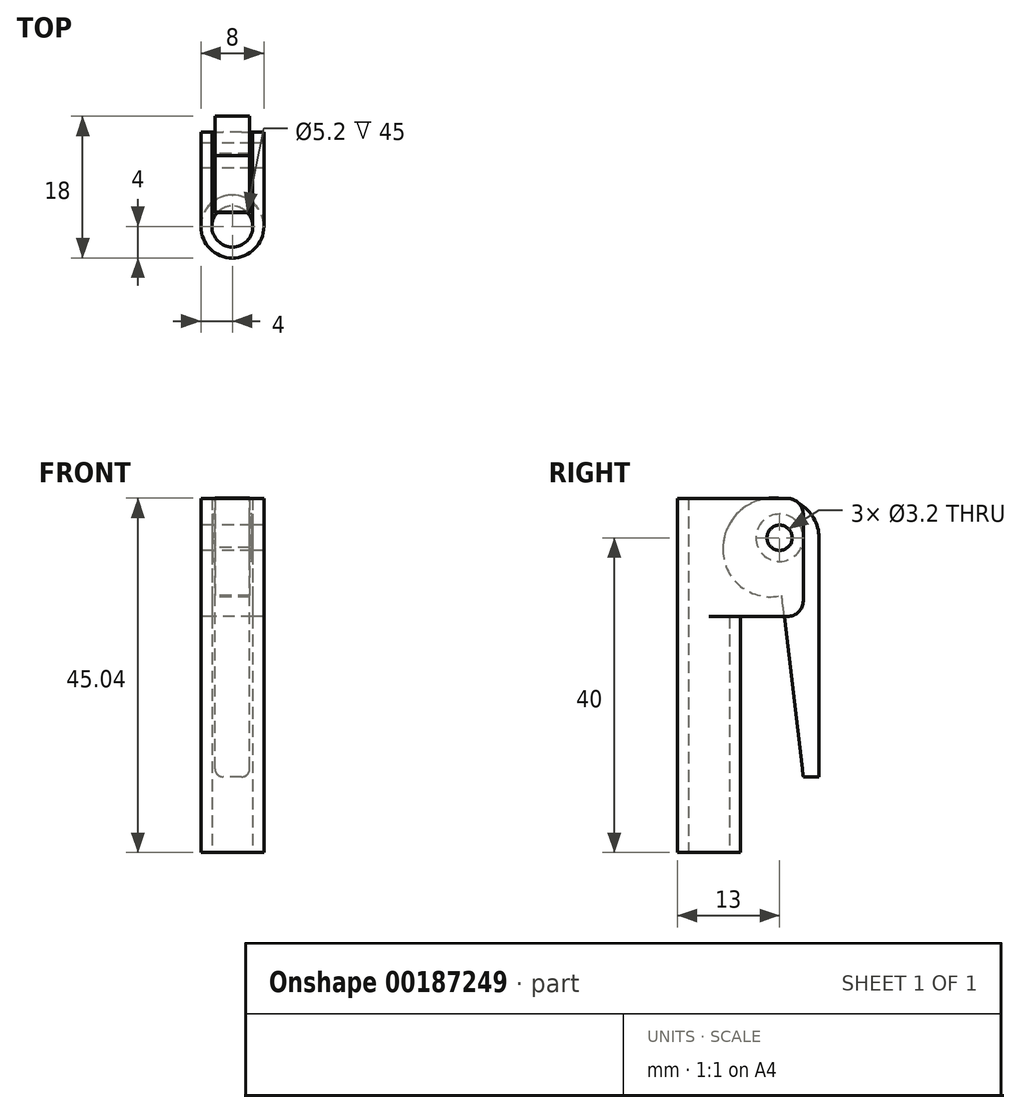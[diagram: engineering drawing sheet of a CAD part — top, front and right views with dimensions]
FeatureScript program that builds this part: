
annotation { "Feature Type Name" : "Feature", "Feature Type Description" : "" }
export const myFeature = defineFeature(function(context is Context, id is Id, definition is map)
    precondition{}
    {
        {
            var Q0;
            Q0=qCreatedBy(makeId("Top.planeOp"),FACE);
            var sketch = newSketch(context, id + "F0", { "sketchPlane" : qUnion([Q0])});
            skCircle(sketch, "E0", {"center": v(0, 0) * mm, "radius": 2.6 * mm});
            skCircle(sketch, "E1", {"center": v(0, 0) * mm, "radius": 4 * mm});
            skLineSegment(sketch, "E2", {"start": v(0, 0) * mm, "end": v(0, 5.84) * mm, "construction": true});
            skSolve(sketch);
        }
        {
            var Q0;
            Q0=makeQuery(id+"F0.imprint","IMPRINT",FACE,{"disambiguationData":[TD([[makeQuery(id+"F0.imprint","IMPRINT",EDGE,{"derivedFrom":sQuery(id+"F0.wireOp",EDGE,"E0")}),-1.0]])]});
            extrude(context, id + "F1", {"entities" : qUnion([Q0]), "depth" : 30 * mm});
        }
        {
            var Q0;
            Q0=makeQuery(id+"F1.opExtrude","CAP_FACE",FACE,{"disambiguationData":[OSD([sQuery(id+"F0.wireOp",EDGE,"E0"),sQuery(id+"F0.wireOp",EDGE,"E1")])],"isStart":false});
            var sketch = newSketch(context, id + "F2", { "sketchPlane" : qUnion([Q0])});
            skArc(sketch, "E3", {"start": v(-2.6, 0) * mm, "mid": v(0, -2.6) * mm, "end": v(2.6, 0) * mm});
            skArc(sketch, "E4", {"start": v(-2.6, 3.04) * mm, "mid": v(0, -4) * mm, "end": v(2.6, 3.04) * mm});
            skLineSegment(sketch, "E5", {"start": v(-4, 0) * mm, "end": v(-4, 12) * mm});
            skLineSegment(sketch, "E6", {"start": v(4, 0) * mm, "end": v(4, 12) * mm});
            skLineSegment(sketch, "E7.0", {"start": v(-2.6, 0) * mm, "end": v(-2.6, 12) * mm});
            skLineSegment(sketch, "E8.0", {"start": v(2.6, 0) * mm, "end": v(2.6, 12) * mm});
            skLineSegment(sketch, "E9", {"start": v(-2.6, 12) * mm, "end": v(-4, 12) * mm});
            skLineSegment(sketch, "E10", {"start": v(4, 12) * mm, "end": v(2.6, 12) * mm});
            skSolve(sketch);
        }
        {
            var Q0;
            {var subQ8=sQuery(id+"F2.wireOp",EDGE,"E3");Q0=makeQuery(id+"F2.imprint","IMPRINT",FACE,{"disambiguationData":[TD([[makeQuery(id+"F2.imprint","IMPRINT",EDGE,{"derivedFrom":subQ8}),-1.0]])]});}
            var Q1;
            {var subQ0=sQuery(id+"F2.wireOp",EDGE,"E6");Q1=makeQuery(id+"F2.imprint","IMPRINT",FACE,{"disambiguationData":[TD([[makeQuery(id+"F2.imprint","IMPRINT",EDGE,{"derivedFrom":subQ0}),1.0]])]});}
            var Q2;
            {var subQ0=sQuery(id+"F2.wireOp",EDGE,"E5");Q2=makeQuery(id+"F2.imprint","IMPRINT",FACE,{"disambiguationData":[TD([[makeQuery(id+"F2.imprint","IMPRINT",EDGE,{"derivedFrom":subQ0}),-1.0]])]});}
            extrude(context, id + "F3", {"entities" : qUnion([Q0, Q1, Q2]), "operationType" : NewBodyOperationType.ADD, "depth" : 15 * mm});
        }
        {
            var Q0;
            Q0=makeQuery(id+"F3.opExtrude","SWEPT_FACE",FACE,{"disambiguationData":[OSD([sQuery(id+"F2.wireOp",EDGE,"E6")])]});
            var sketch = newSketch(context, id + "F4", { "sketchPlane" : qUnion([Q0])});
            skSolve(sketch);
        }
        {
            var Q0;
            {var subQ0=sQuery(id+"F2.wireOp",EDGE,"E6");Q0=makeQuery(id+"F4.imprint","IMPRINT",FACE,{"disambiguationData":[TD([[makeQuery(id+"F4.imprint","IMPRINT",EDGE,{"derivedFrom":makeQuery(id+"F3.opExtrude","CAP_EDGE",EDGE,{"disambiguationData":[OSD([subQ0])],"isStart":true})}),1.0]])]});}
            var sketch = newSketch(context, id + "F5", { "sketchPlane" : qUnion([Q0])});
            skLineSegment(sketch, "E11", {"start": v(4, 0) * mm, "end": v(4, 56.04) * mm, "construction": true});
            skLineSegment(sketch, "E12", {"start": v(0, 50) * mm, "end": v(13.63, 50) * mm, "construction": true});
            skLineSegment(sketch, "E13", {"start": v(4, 40) * mm, "end": v(14, 40) * mm, "construction": true});
            skCircle(sketch, "E14", {"center": v(9, 40) * mm, "radius": 1.6 * mm});
            skSolve(sketch);
        }
        {
            var Q0;
            Q0=sQuery(id+"F5.wireOp",VERTEX,"E14.center");
            var Q1;
            Q1=makeQuery(id+"F1.opExtrude","SWEPT_BODY",BODY,{"disambiguationData":[OSD([sQuery(id+"F0.wireOp",EDGE,"E0"),sQuery(id+"F0.wireOp",EDGE,"E1")])]});
            hole(context, id + "F6", {"style" : HoleStyle.SIMPLE, "endStyle" : HoleEndStyle.THROUGH, "holeDiameter" : 3.2 * mm, "locations" : qUnion([Q0]), "scope" : qUnion([Q1]), "isTappedThrough" : true, "startStyle" : HoleStartStyle.PART});
        }
        {
            var Q0;
            Q0=qCreatedBy(makeId("Right.planeOp"),FACE);
            var sketch = newSketch(context, id + "F7", { "sketchPlane" : qUnion([Q0])});
            skLineSegment(sketch, "E15", {"start": v(9, 0) * mm, "end": v(9, 49.55) * mm, "construction": true});
            skLineSegment(sketch, "E16", {"start": v(0, 40) * mm, "end": v(31.34, 40) * mm, "construction": true});
            skCircle(sketch, "E17", {"center": v(9, 40) * mm, "radius": 1.6 * mm});
            skCircle(sketch, "E18", {"center": v(9, 40) * mm, "radius": 5 * mm});
            skLineSegment(sketch, "E19", {"start": v(12, 9.63) * mm, "end": v(14, 9.63) * mm});
            skLineSegment(sketch, "E20", {"start": v(14, 9.63) * mm, "end": v(14, 40) * mm});
            skLineSegment(sketch, "E21", {"start": v(9.02, 9.48) * mm, "end": v(9, 9.7) * mm});
            skArc(sketch, "E22", {"start": v(6.58, 44.37) * mm, "mid": v(1.95, 37.15) * mm, "end": v(9.27, 32.68) * mm});
            skLineSegment(sketch, "E23", {"start": v(12, 9.63) * mm, "end": v(9, 35) * mm});
            skArc(sketch, "E24", {"start": v(9, 45) * mm, "mid": v(4.02, 43.46) * mm, "end": v(1.8, 38.74) * mm});
            skSolve(sketch);
        }
        {
            var Q0;
            Q0=makeQuery(id+"F7.imprint","IMPRINT",FACE,{"disambiguationData":[TD([[makeQuery(id+"F7.imprint","IMPRINT",EDGE,{"derivedFrom":sQuery(id+"F7.wireOp",EDGE,"E19")}),1.0]])]});
            var Q1;
            Q1=makeQuery(id+"F7.imprint","IMPRINT",FACE,{"disambiguationData":[TD([[makeQuery(id+"F7.imprint","IMPRINT",EDGE,{"derivedFrom":sQuery(id+"F7.wireOp",EDGE,"E17")}),-1.0]])]});
            var Q2;
            {var subQ3=sQuery(id+"F7.wireOp",EDGE,"E22");Q2=makeQuery(id+"F7.imprint","IMPRINT",FACE,{"disambiguationData":[TD([[makeQuery(id+"F7.imprint","IMPRINT",EDGE,{"derivedFrom":subQ3}),1.0]])]});}
            var Q3;
            {var subQ3=sQuery(id+"F7.wireOp",EDGE,"E24");Q3=makeQuery(id+"F7.imprint","IMPRINT",FACE,{"disambiguationData":[TD([[makeQuery(id+"F7.imprint","IMPRINT",EDGE,{"derivedFrom":subQ3}),1.0]])]});}
            extrude(context, id + "F8", {"entities" : qUnion([Q0, Q1, Q2, Q3]), "depth" : 4.4 * mm, "symmetric" : true});
        }
        {
            var Q0;
            Q0=makeQuery(id+"F8.opExtrude","CAP_FACE",FACE,{"disambiguationData":[OSD([sQuery(id+"F7.wireOp",EDGE,"E17"),sQuery(id+"F7.wireOp",EDGE,"E18"),sQuery(id+"F7.wireOp",EDGE,"E19"),sQuery(id+"F7.wireOp",EDGE,"E20"),sQuery(id+"F7.wireOp",EDGE,"HUSRrBSV-6zhb-J2nK-oxZC-g73eNEfcQnkW")])],"isStart":false});
            var sketch = newSketch(context, id + "F9", { "sketchPlane" : qUnion([Q0])});
            skCircle(sketch, "E25", {"center": v(9, 40) * mm, "radius": 3 * mm});
            skSolve(sketch);
        }
        {
            var Q0;
            Q0=makeQuery(id+"F9.imprint","IMPRINT",FACE,{"disambiguationData":[TD([[makeQuery(id+"F9.imprint","IMPRINT",EDGE,{"derivedFrom":sQuery(id+"F9.wireOp",EDGE,"E25")}),1.0]])]});
            extrude(context, id + "F10", {"entities" : qUnion([Q0]), "operationType" : NewBodyOperationType.ADD, "depth" : 0.3 * mm});
        }
        {
            var Q0;
            Q0=makeQuery(id+"F8.opExtrude","CAP_FACE",FACE,{"disambiguationData":[OSD([sQuery(id+"F7.wireOp",EDGE,"E17"),sQuery(id+"F7.wireOp",EDGE,"E18"),sQuery(id+"F7.wireOp",EDGE,"E19"),sQuery(id+"F7.wireOp",EDGE,"E20"),sQuery(id+"F7.wireOp",EDGE,"HUSRrBSV-6zhb-J2nK-oxZC-g73eNEfcQnkW")])],"isStart":true});
            var sketch = newSketch(context, id + "F11", { "sketchPlane" : qUnion([Q0])});
            skCircle(sketch, "E26", {"center": v(-9, 40) * mm, "radius": 3 * mm});
            skSolve(sketch);
        }
        {
            var Q0;
            Q0=makeQuery(id+"F11.imprint","IMPRINT",FACE,{"disambiguationData":[TD([[makeQuery(id+"F11.imprint","IMPRINT",EDGE,{"derivedFrom":sQuery(id+"F11.wireOp",EDGE,"E26")}),1.0]])]});
            extrude(context, id + "F12", {"entities" : qUnion([Q0]), "operationType" : NewBodyOperationType.ADD, "depth" : 0.3 * mm});
        }
        {
            var Q0;
            Q0=makeQuery(id+"F3.opExtrude","CAP_EDGE",EDGE,{"disambiguationData":[OSD([sQuery(id+"F2.wireOp",EDGE,"E9")])],"isStart":false});
            var Q1;
            Q1=makeQuery(id+"F3.opExtrude","CAP_EDGE",EDGE,{"disambiguationData":[OSD([sQuery(id+"F2.wireOp",EDGE,"E10")])],"isStart":false});
            var Q2;
            Q2=makeQuery(id+"F3.opExtrude","CAP_EDGE",EDGE,{"disambiguationData":[OSD([sQuery(id+"F2.wireOp",EDGE,"E10")])],"isStart":true});
            var Q3;
            Q3=makeQuery(id+"F3.opExtrude","CAP_EDGE",EDGE,{"disambiguationData":[OSD([sQuery(id+"F2.wireOp",EDGE,"E9")])],"isStart":true});
            fillet(context, id + "F13", {"entities" : qUnion([Q0, Q1, Q2, Q3]), "radius" : 2 * mm, "tangentPropagation" : true, "allowEdgeOverflow" : false});
        }
        {
            var Q0;
            Q0=makeQuery(id+"F8.opExtrude","CAP_EDGE",EDGE,{"disambiguationData":[OSD([sQuery(id+"F7.wireOp",EDGE,"E19")])],"isStart":true});
            var Q1;
            Q1=makeQuery(id+"F8.opExtrude","CAP_EDGE",EDGE,{"disambiguationData":[OSD([sQuery(id+"F7.wireOp",EDGE,"E19")])],"isStart":false});
            fillet(context, id + "F14", {"entities" : qUnion([Q0, Q1]), "radius" : 1 * mm, "tangentPropagation" : true, "allowEdgeOverflow" : false});
        }
    });
